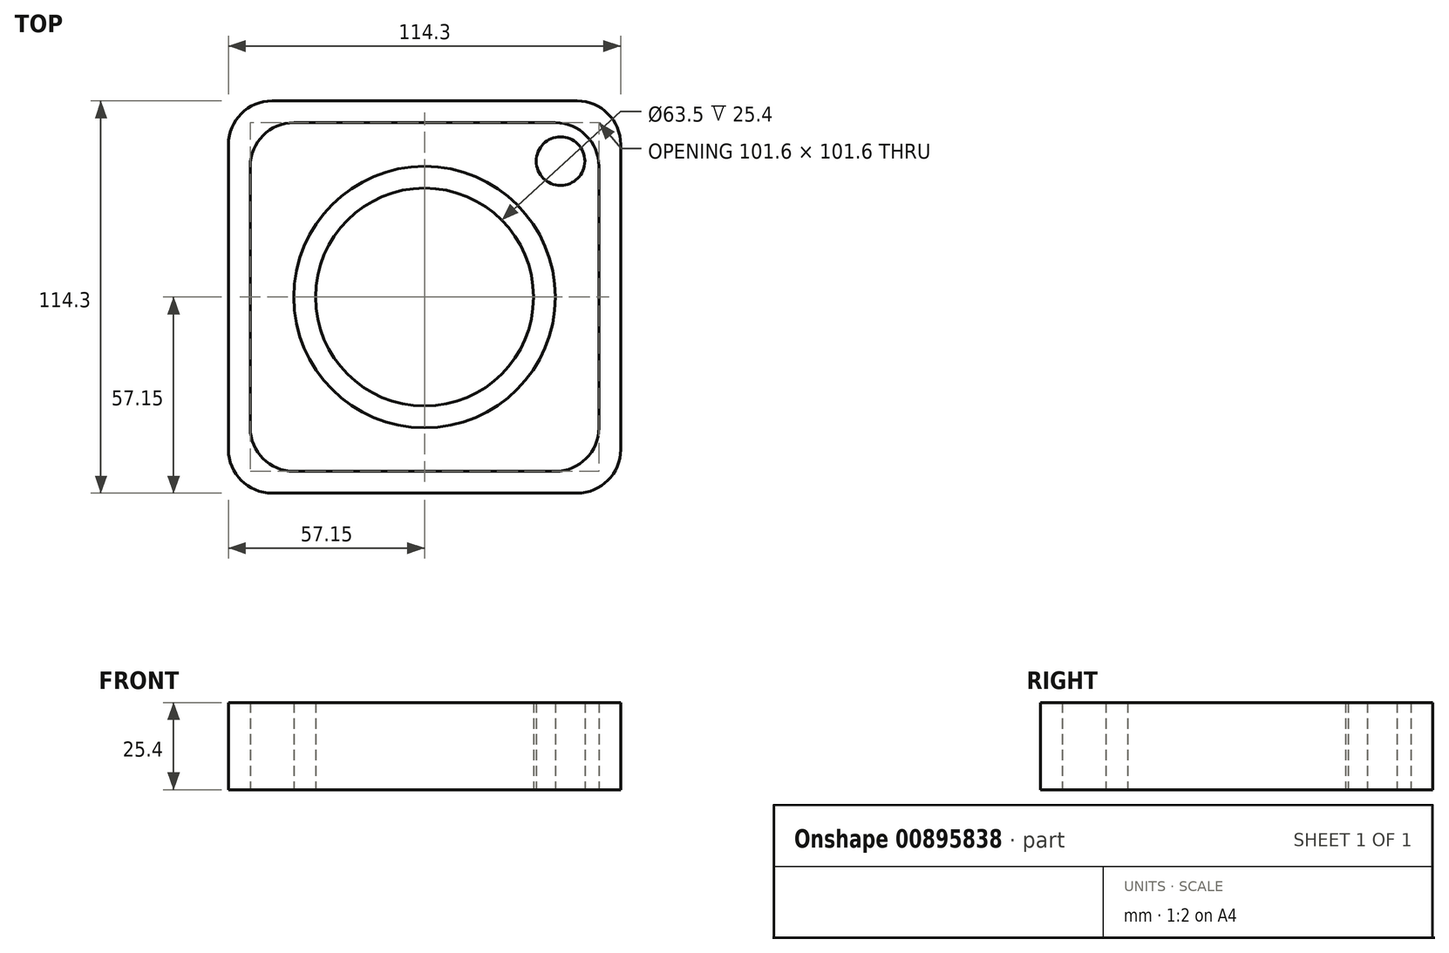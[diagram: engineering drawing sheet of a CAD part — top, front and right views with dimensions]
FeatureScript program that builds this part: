
annotation { "Feature Type Name" : "Feature", "Feature Type Description" : "" }
export const myFeature = defineFeature(function(context is Context, id is Id, definition is map)
    precondition{}
    {
        {
            var Q0;
            Q0=qCreatedBy(makeId("Top.planeOp"),FACE);
            var sketch = newSketch(context, id + "F0", { "sketchPlane" : qUnion([Q0])});
            skLineSegment(sketch, "E0.bottom", {"start": v(50.8, 50.8) * mm, "end": v(-50.8, 50.8) * mm});
            skLineSegment(sketch, "E0.top", {"start": v(50.8, -50.8) * mm, "end": v(-50.8, -50.8) * mm});
            skLineSegment(sketch, "E0.left", {"start": v(50.8, 50.8) * mm, "end": v(50.8, -50.8) * mm});
            skLineSegment(sketch, "E0.right", {"start": v(-50.8, 50.8) * mm, "end": v(-50.8, -50.8) * mm});
            skPoint(sketch, "E0.middle", {"position": v(0, 0) * mm});
            skCircle(sketch, "E1", {"center": v(0, 0) * mm, "radius": 38.1 * mm});
            skCircle(sketch, "E2", {"center": v(0, 0) * mm, "radius": 31.75 * mm});
            skLineSegment(sketch, "E3.bottom", {"start": v(57.15, 57.15) * mm, "end": v(-57.15, 57.15) * mm});
            skLineSegment(sketch, "E3.top", {"start": v(57.15, -57.15) * mm, "end": v(-57.15, -57.15) * mm});
            skLineSegment(sketch, "E3.left", {"start": v(57.15, 57.15) * mm, "end": v(57.15, -57.15) * mm});
            skLineSegment(sketch, "E3.right", {"start": v(-57.15, 57.15) * mm, "end": v(-57.15, -57.15) * mm});
            skCircle(sketch, "E4", {"center": v(39.63, 39.63) * mm, "radius": 7.08 * mm});
            skSolve(sketch);
        }
        {
            var Q0;
            Q0 = qSketchRegion(id + "F0", true);
            var Q1;
            Q1=makeQuery(id+"F0.imprint","IMPRINT",FACE,{"disambiguationData":[TD([[makeQuery(id+"F0.imprint","IMPRINT",EDGE,{"derivedFrom":sQuery(id+"F0.wireOp",EDGE,"E1")}),1.0]])]});
            var Q2;
            Q2=makeQuery(id+"F0.imprint","IMPRINT",FACE,{"disambiguationData":[TD([[makeQuery(id+"F0.imprint","IMPRINT",EDGE,{"derivedFrom":sQuery(id+"F0.wireOp",EDGE,"E4")}),1.0]])]});
            extrude(context, id + "F1", {"entities" : qUnion([Q0, Q1, Q2]), "depth" : 25.4 * mm, "offsetDistance" : 25.4 * mm});
        }
        {
            var Q0;
            Q0=makeQuery(id+"F1.opExtrude","SWEPT_EDGE",EDGE,{"disambiguationData":[OSD([sQuery(id+"F0.wireOp",EDGE,"E3.top"),sQuery(id+"F0.wireOp",EDGE,"E3.right")])]});
            var Q1;
            Q1=makeQuery(id+"F1.opExtrude","SWEPT_EDGE",EDGE,{"disambiguationData":[OSD([sQuery(id+"F0.wireOp",EDGE,"E0.bottom"),sQuery(id+"F0.wireOp",EDGE,"E0.right")])]});
            var Q2;
            Q2=makeQuery(id+"F1.opExtrude","SWEPT_EDGE",EDGE,{"disambiguationData":[OSD([sQuery(id+"F0.wireOp",EDGE,"E0.top"),sQuery(id+"F0.wireOp",EDGE,"E0.right")])]});
            var Q3;
            Q3=makeQuery(id+"F1.opExtrude","SWEPT_EDGE",EDGE,{"disambiguationData":[OSD([sQuery(id+"F0.wireOp",EDGE,"E0.bottom"),sQuery(id+"F0.wireOp",EDGE,"E0.left")])]});
            var Q4;
            Q4=makeQuery(id+"F1.opExtrude","SWEPT_EDGE",EDGE,{"disambiguationData":[OSD([sQuery(id+"F0.wireOp",EDGE,"E3.top"),sQuery(id+"F0.wireOp",EDGE,"E3.left")])]});
            var Q5;
            Q5=makeQuery(id+"F1.opExtrude","SWEPT_EDGE",EDGE,{"disambiguationData":[OSD([sQuery(id+"F0.wireOp",EDGE,"E3.bottom"),sQuery(id+"F0.wireOp",EDGE,"E3.right")])]});
            var Q6;
            Q6=makeQuery(id+"F1.opExtrude","SWEPT_EDGE",EDGE,{"disambiguationData":[OSD([sQuery(id+"F0.wireOp",EDGE,"E3.bottom"),sQuery(id+"F0.wireOp",EDGE,"E3.left")])]});
            var Q7;
            Q7=makeQuery(id+"F1.opExtrude","SWEPT_EDGE",EDGE,{"disambiguationData":[OSD([sQuery(id+"F0.wireOp",EDGE,"E0.top"),sQuery(id+"F0.wireOp",EDGE,"E0.left")])]});
            fillet(context, id + "F2", {"entities" : qUnion([Q0, Q1, Q2, Q3, Q4, Q5, Q6, Q7]), "radius" : 12.7 * mm, "tangentPropagation" : true, "allowEdgeOverflow" : false});
        }
    });
